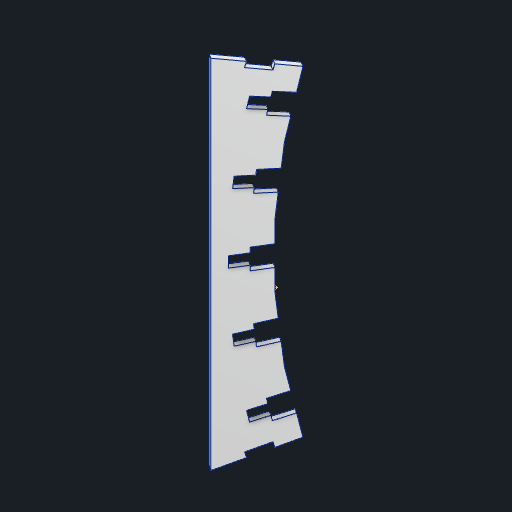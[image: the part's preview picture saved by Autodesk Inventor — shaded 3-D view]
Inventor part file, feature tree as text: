
AUTODESK INVENTOR PART (.ipt)
format: ipt  version: 2023 (Build 270158000, 158)  size: 240,640 bytes
history: native  units: in
note: dims shown in document units (in); Inventor stores cm internally (conversion verified against a paired STEP export)
features: reference x31, other x16, plane x2, extrude x2, sketch x1
ambient origin geometry x8: Origin, YZ Plane, XZ Plane, XY Plane, X Axis, Y Axis, Z Axis, Center Point
bodies: Solid1 (feature_tree)
feature tree (52):
  plane  "Work Plane2"
  extrude  "Extrusion1"  Depth=0.125in TaperAngle=0.0deg
  extrude  "Extrusion2"  Depth=0.125in TaperAngle=0.0deg
  other  "Work Point1"
  plane  "Work Plane1"
  reference  "Reference1"
  reference  "Reference2"
  reference  "Reference3"
  reference  "Reference4"
  reference  "Reference5"
  reference  "Reference6"
  reference  "Reference7"
  reference  "Reference8"
  reference  "Reference9"
  reference  "Reference10"
  sketch  "Sketch3"  dims[d0=1.1in d1=0.125in d2=0.0in d14=0.125in d15=0.0in d16=0.24in d17=0.24in d20=0.24in d21=0.24in d22=0.24in d23=0.24in d24=0.24in d25=0.24in d26=0.24in d27=0.24in]
  reference  "Reference11"
  reference  "Reference12"
  reference  "Reference13"
  reference  "Reference14"
  reference  "Reference15"
  reference  "Reference16"
  reference  "Reference19"
  reference  "Reference20"
  reference  "Reference21"
  reference  "Reference22"
  reference  "Reference23"
  reference  "Reference24"
  reference  "Reference25"
  reference  "Reference26"
  reference  "Reference27"
  reference  "Reference28"
  reference  "Reference29"
  reference  "Reference30"
  reference  "Reference31"
  reference  "Reference32"
  reference  "Reference33"
  other  "<userpath>\Desktop\WaccaController\Wacca Controller\Touch Segment\Touch Segment.iam"
  other  "Touch Segment.iam"
  other  "Touch Fifth:3"
  other  "Touch Fifth:4"
  other  "Touch Fifth:5"
  other  "Touch Fifth:2"
  other  "Touch Fifth:1"
  other  "SidePlate:1"
  other  "SidePlate:2"
  other  "Inner Bracket:1"
  other  "Inner Bracket:3"
  other  "Inner Bracket:2"
  other  "Inner Bracket:4"
  other  "Inner Bracket:5"
  other  "<userpath>\Desktop\Wacca Controller V2\Touch Segment\Touch Segment.iam"
